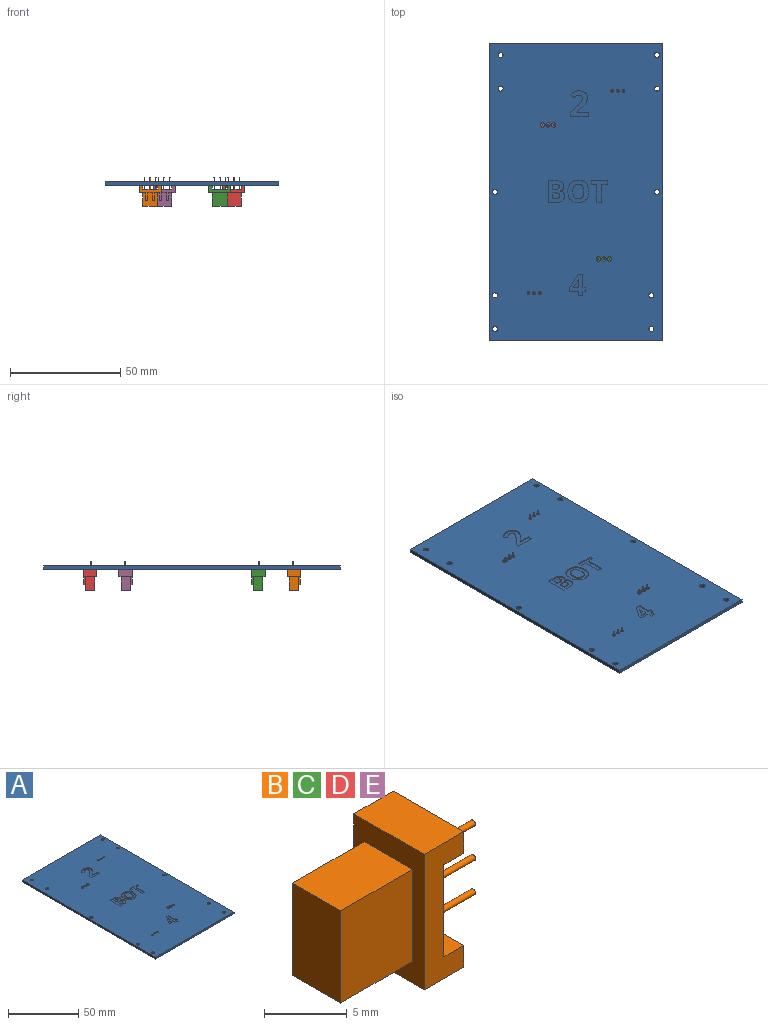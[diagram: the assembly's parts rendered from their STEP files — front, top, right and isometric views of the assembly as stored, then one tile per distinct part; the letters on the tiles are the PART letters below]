
ASSEMBLY  parts=5 mates=4
PART A: 126 faces, bbox 78.7x134.6x1.6 mm
  f0: plane 134.62x78.74mm, normal (0,0,1), area 10265.1mm2, adj f1,f2,f3,f4,f6,f7,f8,f9
  f1: plane 134.62x1.6mm, normal (1,0,0), area 215.4mm2, adj f0,f2,f4,f5
  f2: plane 78.74x1.6mm, normal (0,1,0), area 126mm2, adj f0,f1,f3,f5
  f3: plane 134.62x1.6mm, normal (-1,0,0), area 215.4mm2, adj f0,f2,f4,f5
  f4: plane 78.74x1.6mm, normal (0,-1,0), area 126mm2, adj f0,f1,f3,f5
  f5: plane 134.62x78.74mm, normal (0,0,-1), area 10531.9mm2, adj f1,f2,f3,f4,f6,f7,f8,f9
  f6: cylinder r=1.15mm len=2.3mm, axis (0,0,1), area 11.6mm2, adj f0,f5
  f7: cylinder r=1.15mm len=2.3mm, axis (0,0,1), area 11.6mm2, adj f0,f5
  f8: cylinder r=1.15mm len=2.3mm, axis (0,0,1), area 11.6mm2, adj f0,f5
  f9: cylinder r=1.15mm len=2.3mm, axis (0,0,1), area 11.6mm2, adj f0,f5
  f10: cylinder r=1.15mm len=2.3mm, axis (0,0,1), area 11.6mm2, adj f0,f5
  f11: cylinder r=1.15mm len=2.3mm, axis (0,0,1), area 11.6mm2, adj f0,f5
  f12: cylinder r=1.15mm len=2.3mm, axis (0,0,1), area 11.6mm2, adj f0,f5
  f13: cylinder r=1.15mm len=2.3mm, axis (0,0,1), area 11.6mm2, adj f0,f5
  f14: cylinder r=1.15mm len=2.3mm, axis (0,0,1), area 11.6mm2, adj f0,f5
  f15: cylinder r=1.15mm len=2.3mm, axis (0,0,1), area 11.6mm2, adj f0,f5
  f16: cylinder r=1mm len=2mm, axis (0,0,1), area 10.1mm2, adj f0,f5
  f17: cylinder r=1mm len=2.01mm, axis (0,0,1), area 10.1mm2, adj f0,f5
  f18: cylinder r=1mm len=2.01mm, axis (0,0,1), area 10.1mm2, adj f0,f5
  f19: cylinder r=1mm len=2.01mm, axis (0,0,1), area 10.1mm2, adj f0,f5
  f20: cylinder r=1mm len=2mm, axis (0,0,1), area 10.1mm2, adj f0,f5
  f21: cylinder r=1mm len=2.01mm, axis (0,0,1), area 10.1mm2, adj f0,f5
  f22: plane 8.07x0.5mm, normal (0,1,0), area 4mm2, adj f0,f23,f45,f46
  f23: plane 2.05x0.5mm, normal (-1,0,0), area 1mm2, adj f0,f22,f24,f46
  f24: plane 5.03x0.5mm, normal (0,-1,0), area 2.5mm2, adj f0,f23,f25,f46
  f25: plane 0.5x0.11mm, normal (-1,0,0), area 0.1mm2, adj f0,f24,f26,f46
  f26: plane 1.49x1.4mm, normal (-0.69,0.73,0), area 1mm2, adj f0,f25,f27,f46
  f27: extruded ~2.09x2.07mm, area 1.5mm2, adj f0,f26,f28,f46
  f28: extruded ~1.43x0.87mm, area 0.8mm2, adj f0,f27,f29,f46
  f29: extruded ~1.5x0.5mm, area 0.8mm2, adj f0,f28,f30,f46
  f30: extruded ~1.63x0.5mm, area 0.9mm2, adj f0,f29,f31,f46
  f31: extruded ~1.29x1.11mm, area 0.9mm2, adj f0,f30,f32,f46
  f32: extruded ~1.91x0.5mm, area 1mm2, adj f0,f31,f33,f46
  f33: extruded ~1.48x0.5mm, area 0.7mm2, adj f0,f32,f34,f46
  f34: extruded ~1.22x0.5mm, area 0.7mm2, adj f0,f33,f35,f46
  f35: extruded ~1.41x1.03mm, area 0.9mm2, adj f0,f34,f36,f46
  f36: plane 1.57x1.33mm, normal (0.76,0.65,0), area 1mm2, adj f0,f35,f37,f46
  f37: extruded ~1.32x0.88mm, area 0.8mm2, adj f0,f36,f38,f46
  f38: extruded ~1.3x0.5mm, area 0.7mm2, adj f0,f37,f39,f46
  f39: extruded ~1.02x0.5mm, area 0.6mm2, adj f0,f38,f40,f46
  f40: extruded ~1.03x0.5mm, area 0.6mm2, adj f0,f39,f41,f46
  f41: extruded ~0.9x0.5mm, area 0.5mm2, adj f0,f40,f42,f46
  f42: extruded ~0.94x0.57mm, area 0.6mm2, adj f0,f41,f43,f46
  f43: extruded ~1.83x1.68mm, area 1.2mm2, adj f0,f42,f44,f46
  f44: plane 2.93x2.9mm, normal (0.71,-0.7,0), area 2.1mm2, adj f0,f43,f45,f46
  f45: plane 1.7x0.5mm, normal (1,0,0), area 0.8mm2, adj f0,f22,f44,f46
  f46: plane 11.71x8.1mm, normal (0,0,1), area 49.6mm2, adj f22,f23,f24,f25,f26,f27,f28,f29
  f47: extruded ~2.5x0.63mm, area 1.3mm2, adj f48,f60,f61,f117
  f48: extruded ~2.5x0.64mm, area 1.3mm2, adj f47,f49,f61,f117
  f49: extruded ~1.89x0.84mm, area 1.1mm2, adj f48,f50,f61,f117
  f50: extruded ~3.35x2.5mm, area 2.4mm2, adj f49,f51,f61,f117
  f51: extruded ~3.34x2.52mm, area 2.4mm2, adj f50,f60,f61,f117
  f52: extruded ~3.79x1.22mm, area 2mm2, adj f0,f53,f59,f61
  f53: extruded ~3.78x1.21mm, area 2mm2, adj f0,f52,f54,f61
  f54: extruded ~3.5x1.32mm, area 1.9mm2, adj f0,f53,f55,f61
  f55: extruded ~3.51x1.31mm, area 1.9mm2, adj f0,f54,f56,f61
  f56: extruded ~3.78x1.22mm, area 2mm2, adj f0,f55,f57,f61
  f57: extruded ~3.8x1.22mm, area 2mm2, adj f0,f56,f58,f61
  f58: extruded ~3.5x1.32mm, area 1.9mm2, adj f0,f57,f59,f61
  f59: extruded ~3.5x1.32mm, area 1.9mm2, adj f0,f52,f58,f61
  f60: extruded ~1.88x0.84mm, area 1.1mm2, adj f47,f51,f61,f117
  f61: plane 10.21x9.44mm, normal (0,0,1), area 51.5mm2, adj f47,f48,f49,f50,f51,f52,f53,f54
  f62: plane 1.67x0.5mm, normal (1,0,0), area 0.8mm2, adj f63,f79,f80,f118
  f63: plane 2.37x0.5mm, normal (0,-1,0), area 1.2mm2, adj f62,f64,f80,f118
  f64: plane 2.72x1.8mm, normal (-0.83,0.55,0), area 1.6mm2, adj f63,f65,f80,f118
  f65: extruded ~1.08x0.6mm, area 0.6mm2, adj f64,f66,f80,f118
  f66: plane 0.5x0.05mm, normal (0,1,0), area 0mm2, adj f65,f67,f80,f118
  f67: extruded ~0.92x0.5mm, area 0.5mm2, adj f66,f79,f80,f118
  f68: plane 1.18x0.5mm, normal (0,1,0), area 0.6mm2, adj f0,f69,f78,f80
  f69: plane 1.61x0.5mm, normal (-1,0,0), area 0.8mm2, adj f0,f68,f70,f80
  f70: plane 1.18x0.5mm, normal (0,-1,0), area 0.6mm2, adj f0,f69,f71,f80
  f71: plane 6.18x0.5mm, normal (-1,0,0), area 3.1mm2, adj f0,f70,f72,f80
  f72: plane 1.92x0.5mm, normal (0,-1,0), area 1mm2, adj f0,f71,f73,f80
  f73: plane 6.35x4.31mm, normal (0.83,-0.56,0), area 3.8mm2, adj f0,f72,f74,f80
  f74: plane 1.45x0.5mm, normal (1,0,0), area 0.7mm2, adj f0,f73,f75,f80
  f75: plane 4.2x0.5mm, normal (0,1,0), area 2.1mm2, adj f0,f74,f76,f80
  f76: plane 2.04x0.5mm, normal (1,0,0), area 1mm2, adj f0,f75,f77,f80
  f77: plane 2.03x0.5mm, normal (0,1,0), area 1mm2, adj f0,f76,f78,f80
  f78: plane 2.04x0.5mm, normal (-1,0,0), area 1mm2, adj f0,f68,f77,f80
  f79: extruded ~1.21x0.5mm, area 0.6mm2, adj f62,f67,f80,f118
  f80: plane 9.83x7.41mm, normal (0,0,1), area 36.6mm2, adj f62,f63,f64,f65,f66,f67,f68,f69
  f81: plane 2.58x0.5mm, normal (-1,0,0), area 1.3mm2, adj f82,f105,f106,f119
  f82: plane 1.3x0.5mm, normal (0,1,0), area 0.7mm2, adj f81,f83,f106,f119
  f83: extruded ~1.76x1.24mm, area 1.2mm2, adj f82,f84,f106,f119
  f84: extruded ~1.02x0.5mm, area 0.6mm2, adj f83,f85,f106,f119
  f85: extruded ~1.28x0.5mm, area 0.7mm2, adj f84,f105,f106,f119
  f86: plane 1.22x0.5mm, normal (0,-1,0), area 0.6mm2, adj f87,f103,f106,f107
  f87: plane 2.21x0.5mm, normal (-1,0,0), area 1.1mm2, adj f86,f88,f106,f107
  f88: plane 1.1x0.5mm, normal (0,1,0), area 0.6mm2, adj f87,f89,f106,f107
  f89: extruded ~1.32x0.5mm, area 0.7mm2, adj f88,f90,f106,f107
  f90: extruded ~0.82x0.5mm, area 0.5mm2, adj f89,f91,f106,f107
  f91: extruded ~0.87x0.5mm, area 0.5mm2, adj f90,f103,f106,f107
  f92: plane 3.09x0.5mm, normal (0,-1,0), area 1.5mm2, adj f0,f93,f104,f106
  f93: plane 9.92x0.5mm, normal (1,0,0), area 5mm2, adj f0,f92,f94,f106
  f94: plane 3.71x0.5mm, normal (0,1,0), area 1.9mm2, adj f0,f93,f95,f106
  f95: extruded ~2.66x0.76mm, area 1.4mm2, adj f0,f94,f96,f106
  f96: extruded ~2.12x0.98mm, area 1.2mm2, adj f0,f95,f97,f106
  f97: extruded ~1.53x0.5mm, area 0.8mm2, adj f0,f96,f98,f106
  f98: extruded ~1.36x0.79mm, area 0.8mm2, adj f0,f97,f99,f106
  f99: plane 0.5x0.07mm, normal (-1,0,0), area 0mm2, adj f0,f98,f100,f106
  f100: extruded ~1.11x0.68mm, area 0.7mm2, adj f0,f99,f101,f106
  f101: extruded ~1.46x0.5mm, area 0.8mm2, adj f0,f100,f102,f106
  f102: extruded ~1.91x0.95mm, area 1.1mm2, adj f0,f101,f104,f106
  f103: extruded ~1.24x0.5mm, area 0.6mm2, adj f86,f91,f106,f107
  f104: extruded ~3.06x0.6mm, area 1.6mm2, adj f0,f92,f102,f106
  f105: plane 1.37x0.5mm, normal (0,-1,0), area 0.7mm2, adj f81,f85,f106,f119
  f106: plane 9.92x7.35mm, normal (0,0,1), area 53.6mm2, adj f81,f82,f83,f84,f85,f86,f87,f88
  f107: plane 2.84x2.21mm, normal (0,0,1), area 5.7mm2, adj f86,f87,f88,f89,f90,f91,f103
  f108: plane 2.1x0.5mm, normal (0,1,0), area 1.1mm2, adj f0,f109,f115,f116
  f109: plane 8.17x0.5mm, normal (-1,0,0), area 4.1mm2, adj f0,f108,f110,f116
  f110: plane 2.69x0.5mm, normal (0,1,0), area 1.3mm2, adj f0,f109,f111,f116
  f111: plane 1.75x0.5mm, normal (-1,0,0), area 0.9mm2, adj f0,f110,f112,f116
  f112: plane 7.49x0.5mm, normal (0,-1,0), area 3.7mm2, adj f0,f111,f113,f116
  f113: plane 1.75x0.5mm, normal (1,0,0), area 0.9mm2, adj f0,f112,f114,f116
  f114: plane 2.69x0.5mm, normal (0,1,0), area 1.3mm2, adj f0,f113,f115,f116
  f115: plane 8.17x0.5mm, normal (1,0,0), area 4.1mm2, adj f0,f108,f114,f116
  f116: plane 9.92x7.49mm, normal (0,0,1), area 30.3mm2, adj f108,f109,f110,f111,f112,f113,f114,f115
  f117: plane 6.69x5.03mm, normal (0,0,1), area 28mm2, adj f47,f48,f49,f50,f51,f60
  f118: plane 3.8x2.46mm, normal (0,0,1), area 4.3mm2, adj f62,f63,f64,f65,f66,f67,f79
  f119: plane 3.06x2.58mm, normal (0,0,1), area 7.2mm2, adj f81,f82,f83,f84,f85,f105
  f120: cylinder r=0.64mm len=1.6mm, axis (0,0,1), area 6.4mm2, adj f0,f5
  f121: cylinder r=0.64mm len=1.6mm, axis (0,0,1), area 6.4mm2, adj f0,f5
  f122: cylinder r=0.64mm len=1.6mm, axis (0,0,1), area 6.4mm2, adj f0,f5
  f123: cylinder r=0.64mm len=1.6mm, axis (0,0,1), area 6.4mm2, adj f0,f5
  f124: cylinder r=0.64mm len=1.6mm, axis (0,0,1), area 6.4mm2, adj f0,f5
  f125: cylinder r=0.64mm len=1.6mm, axis (0,0,1), area 6.4mm2, adj f0,f5
PART B: 28 faces, bbox 13x6x10 mm
  f0: plane 6x3.37mm, normal (0,0,-1), area 20.2mm2, adj f6,f7,f8,f10
  f1: plane 6.8x6.13mm, normal (0,1,0), area 34.7mm2, adj f2,f5,f10,f20,f21,f22,f23,f24
  f2: plane 6.8x4.1mm, normal (-1,0,0), area 27.9mm2, adj f1,f3,f26,f27
  f3: plane 6.8x6.13mm, normal (0,-1,0), area 41.7mm2, adj f2,f10,f26,f27
  f4: plane 6x3.37mm, normal (0,0,1), area 20.2mm2, adj f7,f8,f9,f10
  f5: plane 2x0.9mm, normal (-1,0,0), area 1.8mm2, adj f1,f8,f20,f24
  f6: plane 6x1.6mm, normal (1,0,0), area 9.6mm2, adj f0,f7,f8,f12
  f7: plane 10x3.37mm, normal (0,-1,0), area 22.1mm2, adj f0,f4,f6,f9,f10,f11,f12,f13
  f8: plane 10x6.87mm, normal (0,1,0), area 29.1mm2, adj f0,f4,f5,f6,f9,f10,f11,f12
  f9: plane 6x1.6mm, normal (1,0,0), area 9.6mm2, adj f4,f7,f8,f11
  f10: plane 10x6mm, normal (-1,0,0), area 28.5mm2, adj f0,f1,f3,f4,f7,f8,f21,f23
  f11: plane 6x1.7mm, normal (0,0,-1), area 10.2mm2, adj f7,f8,f9,f13
  f12: plane 6x1.7mm, normal (0,0,1), area 10.2mm2, adj f6,f7,f8,f13
  f13: plane 6.8x6mm, normal (1,0,0), area 40.4mm2, adj f7,f8,f11,f12,f14,f16,f18
  f14: cylinder r=0.2mm len=5.2mm, axis (-1,0,0), area 6.7mm2, adj f13,f15
  f15: plane 0.41x0.41mm, normal (1,0,0), area 0.1mm2, adj f14
  f16: cylinder r=0.2mm len=5.2mm, axis (-1,0,0), area 6.5mm2, adj f13,f17
  f17: plane 0.4x0.4mm, normal (1,0,0), area 0.1mm2, adj f16
  f18: cylinder r=0.2mm len=5.2mm, axis (-1,0,0), area 6.5mm2, adj f13,f19
  f19: plane 0.4x0.4mm, normal (1,0,0), area 0.1mm2, adj f18
  f20: plane 3.5x0.9mm, normal (0,0,-1), area 3.1mm2, adj f1,f5,f8,f22
  f21: plane 3.5x0.9mm, normal (0,0,1), area 3.1mm2, adj f1,f8,f10,f22
  f22: plane 1x0.9mm, normal (-1,0,0), area 0.9mm2, adj f1,f8,f20,f21
  f23: plane 3.5x0.9mm, normal (0,0,-1), area 3.1mm2, adj f1,f8,f10,f25
  f24: plane 3.5x0.9mm, normal (0,0,1), area 3.1mm2, adj f1,f5,f8,f25
  f25: plane 1x0.9mm, normal (-1,0,0), area 0.9mm2, adj f1,f8,f23,f24
  f26: plane 6.13x4.1mm, normal (0,0,1), area 25.1mm2, adj f1,f2,f3,f10
  f27: plane 6.13x4.1mm, normal (0,0,-1), area 25.1mm2, adj f1,f2,f3,f10
PART C: same geometry as B
PART D: same geometry as B
PART E: same geometry as B
PLACE A t=(-25.42,20.98,-14.18)mm
PLACE B rot(axis=(0.71,0,0.71),180deg) t=(-88.84,-90.6,-23.68)mm
PLACE C rot(axis=(0,-1,0),90deg) t=(-47.09,-78.51,-23.68)mm
PLACE D rot(axis=(0,-1,0),90deg) t=(-40.74,-2.05,-23.68)mm
PLACE E rot(axis=(0.71,0,0.71),180deg) t=(-82.49,-14.15,-23.68)mm
MATE fastened D.f16 <-> A.f120  axis (0,0,1) through (-45.74,-0.35,-10.68)mm
MATE fastened C.f16 <-> A.f20  axis (0,0,1) through (-52.09,-76.81,-10.68)mm
MATE fastened B.f16 <-> A.f124  axis (0,0,1) through (-83.84,-92.3,-10.68)mm
MATE fastened E.f16 <-> A.f16  axis (0,0,1) through (-77.49,-15.85,-10.68)mm
